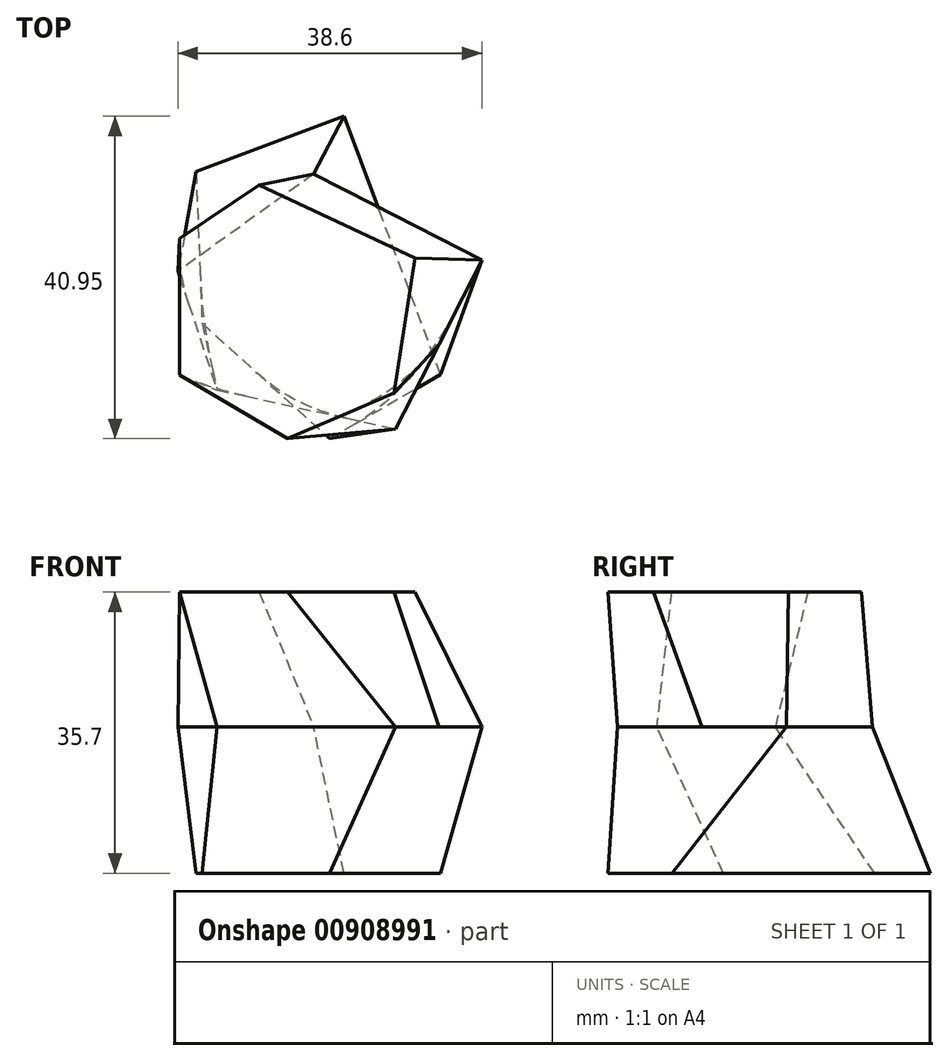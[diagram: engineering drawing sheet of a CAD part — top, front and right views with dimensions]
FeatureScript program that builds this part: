
annotation { "Feature Type Name" : "Feature", "Feature Type Description" : "" }
export const myFeature = defineFeature(function(context is Context, id is Id, definition is map)
    precondition{}
    {
        {
            var Q0;
            Q0=qCreatedBy(makeId("Top.planeOp"),FACE);
            var sketch = newSketch(context, id + "F0", { "sketchPlane" : qUnion([Q0])});
            skLineSegment(sketch, "E0", {"start": v(-10.88, 0) * mm, "end": v(5.32, -14.65) * mm});
            skLineSegment(sketch, "E1", {"start": v(5.32, -14.65) * mm, "end": v(19.44, -6.5) * mm});
            skLineSegment(sketch, "E2", {"start": v(19.44, -6.5) * mm, "end": v(7.16, 26.29) * mm});
            skLineSegment(sketch, "E3", {"start": v(7.16, 26.29) * mm, "end": v(-11.64, 19.24) * mm});
            skLineSegment(sketch, "E4", {"start": v(-11.64, 19.24) * mm, "end": v(-10.88, 0) * mm});
            skSolve(sketch);
        }
        {
            var Q0;
            Q0=qCreatedBy(makeId("Top.planeOp"),FACE);
            cPlane(context, id + "F1", {"entities" : qUnion([Q0]), "cplaneType" : CPlaneType.OFFSET, "offset" : 18.6 * mm, "width" : 150 * mm, "height" : 150 * mm});
        }
        {
            var Q0;
            Q0=qCreatedBy(makeId("Top.planeOp"),FACE);
            cPlane(context, id + "F2", {"entities" : qUnion([Q0]), "cplaneType" : CPlaneType.OFFSET, "offset" : 35.7 * mm, "width" : 150 * mm, "height" : 150 * mm});
        }
        {
            var Q0;
            Q0=qCreatedBy(id+"F1.planeOp",FACE);
            var sketch = newSketch(context, id + "F3", { "sketchPlane" : qUnion([Q0])});
            skLineSegment(sketch, "E5", {"start": v(-8.98, -8.46) * mm, "end": v(13.73, -13.42) * mm});
            skLineSegment(sketch, "E6", {"start": v(13.73, -13.42) * mm, "end": v(24.67, 8.05) * mm});
            skLineSegment(sketch, "E7", {"start": v(24.67, 8.05) * mm, "end": v(3.29, 18.95) * mm});
            skLineSegment(sketch, "E8", {"start": v(3.29, 18.95) * mm, "end": v(-13.93, 6.6) * mm});
            skLineSegment(sketch, "E9", {"start": v(-13.93, 6.6) * mm, "end": v(-8.98, -8.46) * mm});
            skSolve(sketch);
        }
        {
            var Q0;
            Q0=qCreatedBy(id+"F2.planeOp",FACE);
            var sketch = newSketch(context, id + "F4", { "sketchPlane" : qUnion([Q0])});
            skLineSegment(sketch, "E10", {"start": v(-13.73, -6.6) * mm, "end": v(0, -14.66) * mm});
            skLineSegment(sketch, "E11", {"start": v(0, -14.66) * mm, "end": v(13.52, -8.88) * mm});
            skLineSegment(sketch, "E12", {"start": v(13.52, -8.88) * mm, "end": v(16.2, 8.26) * mm});
            skLineSegment(sketch, "E13", {"start": v(16.2, 8.26) * mm, "end": v(-3.61, 17.55) * mm});
            skLineSegment(sketch, "E14", {"start": v(-3.61, 17.55) * mm, "end": v(-13.73, 10.73) * mm});
            skLineSegment(sketch, "E15", {"start": v(-13.73, 10.73) * mm, "end": v(-13.73, -6.6) * mm});
            skSolve(sketch);
        }
        {
            var Q0;
            Q0=makeQuery(id+"F0.imprint","IMPRINT",FACE,{"disambiguationData":[TD([[makeQuery(id+"F0.imprint","IMPRINT",EDGE,{"derivedFrom":sQuery(id+"F0.wireOp",EDGE,"E0")}),1.0]])]});
            var Q1;
            Q1=makeQuery(id+"F3.imprint","IMPRINT",FACE,{"disambiguationData":[TD([[makeQuery(id+"F3.imprint","IMPRINT",EDGE,{"derivedFrom":sQuery(id+"F3.wireOp",EDGE,"E5")}),1.0]])]});
            loft(context, id + "F5", {"sheetProfilesArray" : [{ "sheetProfileEntities" : qUnion([Q0]) }, { "sheetProfileEntities" : qUnion([Q1]) }]});
        }
        {
            var Q1;
            Q1=makeQuery(id+"F4.imprint","IMPRINT",FACE,{"disambiguationData":[TD([[makeQuery(id+"F4.imprint","IMPRINT",EDGE,{"derivedFrom":sQuery(id+"F4.wireOp",EDGE,"E10")}),1.0]])]});
            var Q2;
            Q2=makeQuery(id+"F5.opLoft","CAP_FACE",FACE,{"disambiguationData":[OSD([makeQuery(id+"F3.imprint","IMPRINT",FACE,{"disambiguationData":[TD([[makeQuery(id+"F3.imprint","IMPRINT",EDGE,{"derivedFrom":sQuery(id+"F3.wireOp",EDGE,"E5")}),1.0]])]})])],"isStart":true});
            loft(context, id + "F6", {"operationType" : NewBodyOperationType.ADD, "sheetProfilesArray" : [{ "sheetProfileEntities" : qUnion([Q1]) }, { "sheetProfileEntities" : qUnion([Q2]) }]});
        }
    });
